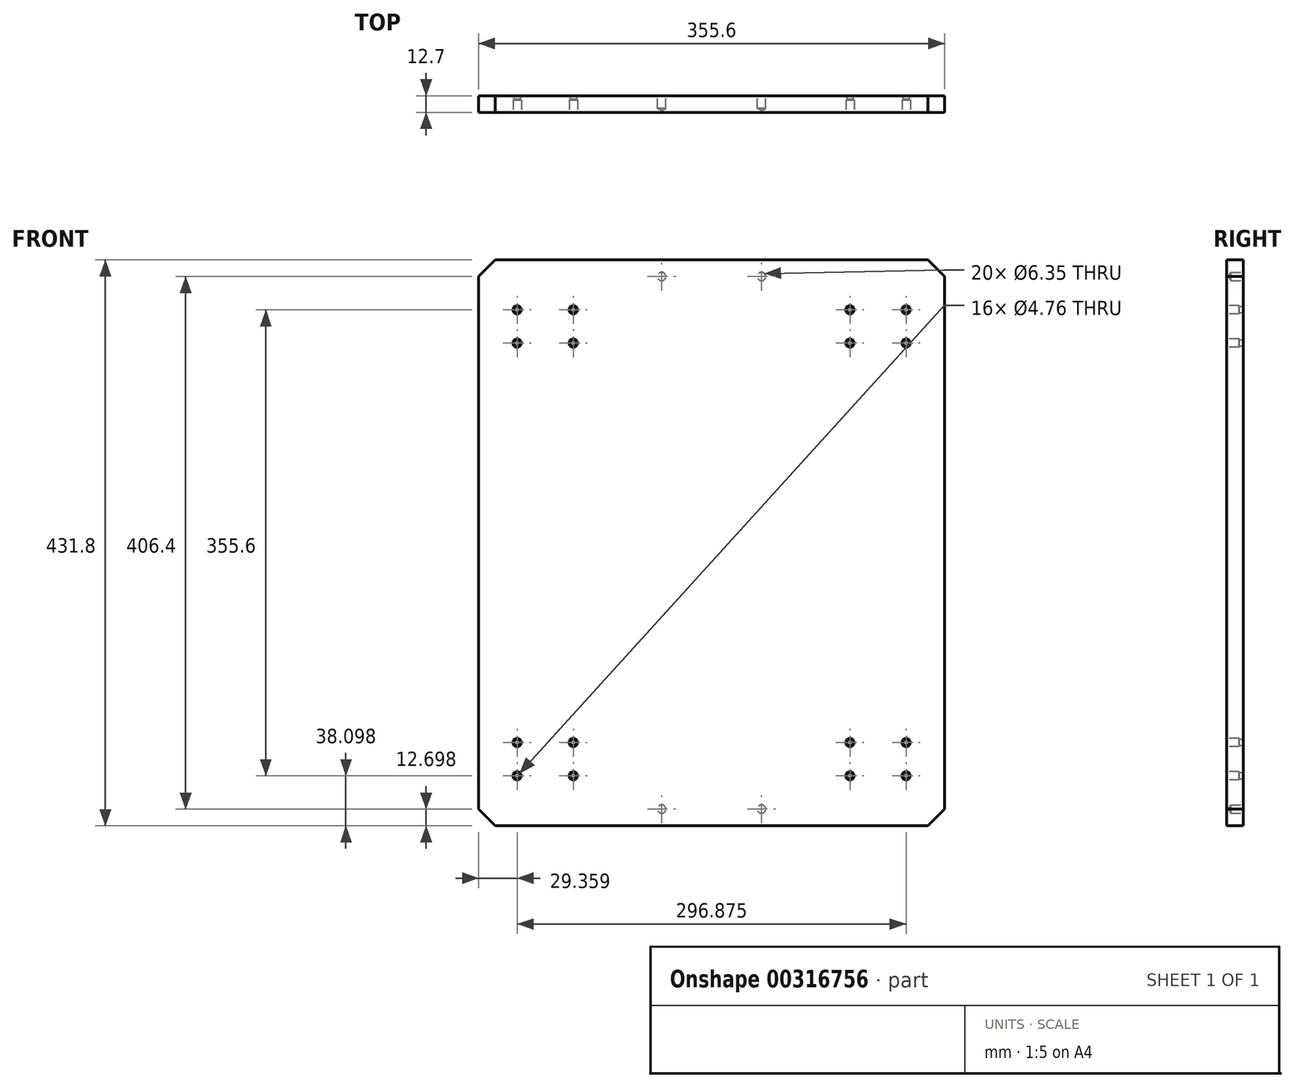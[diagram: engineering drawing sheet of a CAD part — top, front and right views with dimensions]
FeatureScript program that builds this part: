
annotation { "Feature Type Name" : "Feature", "Feature Type Description" : "" }
export const myFeature = defineFeature(function(context is Context, id is Id, definition is map)
    precondition{}
    {
        {
            var Q0;
            Q0=qCreatedBy(makeId("Front.planeOp"),FACE);
            var sketch = newSketch(context, id + "F0", { "sketchPlane" : qUnion([Q0])});
            skLineSegment(sketch, "E0.bottom", {"start": v(-92.04, 358.08) * mm, "end": v(263.56, 358.08) * mm});
            skLineSegment(sketch, "E0.top", {"start": v(-92.04, -73.72) * mm, "end": v(263.56, -73.72) * mm});
            skLineSegment(sketch, "E0.left", {"start": v(-92.04, 358.08) * mm, "end": v(-92.04, -73.72) * mm});
            skLineSegment(sketch, "E0.right", {"start": v(263.56, 358.08) * mm, "end": v(263.56, -73.72) * mm});
            skSolve(sketch);
        }
        {
            var Q0;
            Q0=makeQuery(id+"F0.imprint","IMPRINT",FACE,{"disambiguationData":[TD([[makeQuery(id+"F0.imprint","IMPRINT",EDGE,{"derivedFrom":sQuery(id+"F0.wireOp",EDGE,"E0.bottom")}),-1.0]])]});
            extrude(context, id + "F1", {"entities" : qUnion([Q0]), "depth" : 12.7 * mm});
        }
        {
            var Q0;
            Q0=makeQuery(id+"F1.opExtrude","CAP_FACE",FACE,{"disambiguationData":[OSD([sQuery(id+"F0.wireOp",EDGE,"E0.bottom"),sQuery(id+"F0.wireOp",EDGE,"E0.top"),sQuery(id+"F0.wireOp",EDGE,"E0.left"),sQuery(id+"F0.wireOp",EDGE,"E0.right")])],"isStart":false});
            var sketch = newSketch(context, id + "F2", { "sketchPlane" : qUnion([Q0])});
            skPoint(sketch, "E1", {"position": v(-62.68, -10.22) * mm});
            skPoint(sketch, "E2", {"position": v(-19.8, -35.62) * mm});
            skPoint(sketch, "E3", {"position": v(-62.68, -35.62) * mm});
            skPoint(sketch, "E4", {"position": v(-19.8, -10.22) * mm});
            skLineSegment(sketch, "E5", {"start": v(85.76, 358.08) * mm, "end": v(85.76, -73.72) * mm, "construction": true});
            skPoint(sketch, "E6.MirrorP", {"position": v(191.32, -10.22) * mm});
            skPoint(sketch, "E7.MirrorP", {"position": v(191.32, -35.62) * mm});
            skPoint(sketch, "E8.MirrorP", {"position": v(234.2, -10.22) * mm});
            skPoint(sketch, "E9.MirrorP", {"position": v(234.2, -35.62) * mm});
            skLineSegment(sketch, "E10", {"start": v(-92.04, 142.18) * mm, "end": v(263.56, 142.18) * mm, "construction": true});
            skPoint(sketch, "E11.MirrorP", {"position": v(-19.8, 294.58) * mm});
            skPoint(sketch, "E12.MirrorP", {"position": v(-19.8, 319.98) * mm});
            skPoint(sketch, "E13.MirrorP", {"position": v(-62.68, 319.98) * mm});
            skPoint(sketch, "E14.MirrorP", {"position": v(-62.68, 294.58) * mm});
            skPoint(sketch, "E15.MirrorP", {"position": v(191.32, 294.58) * mm});
            skPoint(sketch, "E16.MirrorP", {"position": v(234.2, 294.58) * mm});
            skPoint(sketch, "E17.MirrorP", {"position": v(234.2, 319.98) * mm});
            skPoint(sketch, "E18.MirrorP", {"position": v(191.32, 319.98) * mm});
            skSolve(sketch);
        }
        {
            var Q0;
            Q0=sQuery(id+"F2.wireOp",VERTEX,"E13.MirrorP");
            var Q1;
            Q1=sQuery(id+"F2.wireOp",VERTEX,"E14.MirrorP");
            var Q2;
            Q2=sQuery(id+"F2.wireOp",VERTEX,"E11.MirrorP");
            var Q3;
            Q3=sQuery(id+"F2.wireOp",VERTEX,"E12.MirrorP");
            var Q4;
            Q4=sQuery(id+"F2.wireOp",VERTEX,"E15.MirrorP");
            var Q5;
            Q5=sQuery(id+"F2.wireOp",VERTEX,"E16.MirrorP");
            var Q6;
            Q6=sQuery(id+"F2.wireOp",VERTEX,"E17.MirrorP");
            var Q7;
            Q7=sQuery(id+"F2.wireOp",VERTEX,"E18.MirrorP");
            var Q8;
            Q8=sQuery(id+"F2.wireOp",VERTEX,"E4");
            var Q9;
            Q9=sQuery(id+"F2.wireOp",VERTEX,"E1");
            var Q10;
            Q10=sQuery(id+"F2.wireOp",VERTEX,"E3");
            var Q11;
            Q11=sQuery(id+"F2.wireOp",VERTEX,"E2");
            var Q12;
            Q12=sQuery(id+"F2.wireOp",VERTEX,"E7.MirrorP");
            var Q13;
            Q13=sQuery(id+"F2.wireOp",VERTEX,"E9.MirrorP");
            var Q14;
            Q14=sQuery(id+"F2.wireOp",VERTEX,"E8.MirrorP");
            var Q15;
            Q15=sQuery(id+"F2.wireOp",VERTEX,"E6.MirrorP");
            var Q16;
            Q16=makeQuery(id+"F1.opExtrude","SWEPT_BODY",BODY,{"disambiguationData":[OSD([sQuery(id+"F0.wireOp",EDGE,"E0.bottom"),sQuery(id+"F0.wireOp",EDGE,"E0.top"),sQuery(id+"F0.wireOp",EDGE,"E0.left"),sQuery(id+"F0.wireOp",EDGE,"E0.right")])]});
            hole(context, id + "F3", {"style" : HoleStyle.SIMPLE, "endStyle" : HoleEndStyle.THROUGH, "holeDiameter" : 4.76 * mm, "tappedDepth" : 12.7 * mm, "tapClearance" : 3, "locations" : qUnion([Q0, Q1, Q2, Q3, Q4, Q5, Q6, Q7, Q8, Q9, Q10, Q11, Q12, Q13, Q14, Q15]), "scope" : qUnion([Q16])});
        }
        {
            var Q0;
            Q0=sQuery(id+"F2.wireOp",VERTEX,"E13.MirrorP");
            var Q1;
            Q1=sQuery(id+"F2.wireOp",VERTEX,"E12.MirrorP");
            var Q2;
            Q2=sQuery(id+"F2.wireOp",VERTEX,"E14.MirrorP");
            var Q3;
            Q3=sQuery(id+"F2.wireOp",VERTEX,"E11.MirrorP");
            var Q4;
            Q4=sQuery(id+"F2.wireOp",VERTEX,"E15.MirrorP");
            var Q5;
            Q5=sQuery(id+"F2.wireOp",VERTEX,"E18.MirrorP");
            var Q6;
            Q6=sQuery(id+"F2.wireOp",VERTEX,"E17.MirrorP");
            var Q7;
            Q7=sQuery(id+"F2.wireOp",VERTEX,"E16.MirrorP");
            var Q8;
            Q8=sQuery(id+"F2.wireOp",VERTEX,"E4");
            var Q9;
            Q9=sQuery(id+"F2.wireOp",VERTEX,"E2");
            var Q10;
            Q10=sQuery(id+"F2.wireOp",VERTEX,"E3");
            var Q11;
            Q11=sQuery(id+"F2.wireOp",VERTEX,"E1");
            var Q12;
            Q12=sQuery(id+"F2.wireOp",VERTEX,"E6.MirrorP");
            var Q13;
            Q13=sQuery(id+"F2.wireOp",VERTEX,"E8.MirrorP");
            var Q14;
            Q14=sQuery(id+"F2.wireOp",VERTEX,"E9.MirrorP");
            var Q15;
            Q15=sQuery(id+"F2.wireOp",VERTEX,"E7.MirrorP");
            var Q16;
            Q16=makeQuery(id+"F1.opExtrude","SWEPT_BODY",BODY,{"disambiguationData":[OSD([sQuery(id+"F0.wireOp",EDGE,"E0.bottom"),sQuery(id+"F0.wireOp",EDGE,"E0.top"),sQuery(id+"F0.wireOp",EDGE,"E0.left"),sQuery(id+"F0.wireOp",EDGE,"E0.right")])]});
            hole(context, id + "F4", {"style" : HoleStyle.SIMPLE, "endStyle" : HoleEndStyle.BLIND, "holeDiameter" : 6.35 * mm, "holeDepth" : 9.52 * mm, "tappedDepth" : 12.7 * mm, "tapClearance" : 3, "locations" : qUnion([Q0, Q1, Q2, Q3, Q4, Q5, Q6, Q7, Q8, Q9, Q10, Q11, Q12, Q13, Q14, Q15]), "scope" : qUnion([Q16])});
        }
        {
            var Q0;
            Q0=makeQuery(id+"F1.opExtrude","SWEPT_EDGE",EDGE,{"disambiguationData":[OSD([sQuery(id+"F0.wireOp",EDGE,"E0.bottom"),sQuery(id+"F0.wireOp",EDGE,"E0.left")])]});
            var Q1;
            Q1=makeQuery(id+"F1.opExtrude","SWEPT_EDGE",EDGE,{"disambiguationData":[OSD([sQuery(id+"F0.wireOp",EDGE,"E0.bottom"),sQuery(id+"F0.wireOp",EDGE,"E0.right")])]});
            var Q2;
            Q2=makeQuery(id+"F1.opExtrude","SWEPT_EDGE",EDGE,{"disambiguationData":[OSD([sQuery(id+"F0.wireOp",EDGE,"E0.top"),sQuery(id+"F0.wireOp",EDGE,"E0.right")])]});
            var Q3;
            Q3=makeQuery(id+"F1.opExtrude","SWEPT_EDGE",EDGE,{"disambiguationData":[OSD([sQuery(id+"F0.wireOp",EDGE,"E0.top"),sQuery(id+"F0.wireOp",EDGE,"E0.left")])]});
            chamfer(context, id + "F5", {"entities" : qUnion([Q0, Q1, Q2, Q3]), "width" : 12.7 * mm, "tangentPropagation" : true});
        }
        {
            var Q0;
            Q0=makeQuery(id+"F1.opExtrude","CAP_FACE",FACE,{"disambiguationData":[OSD([sQuery(id+"F0.wireOp",EDGE,"E0.bottom"),sQuery(id+"F0.wireOp",EDGE,"E0.top"),sQuery(id+"F0.wireOp",EDGE,"E0.left"),sQuery(id+"F0.wireOp",EDGE,"E0.right")])],"isStart":true});
            var sketch = newSketch(context, id + "F6", { "sketchPlane" : qUnion([Q0])});
            skPoint(sketch, "E19", {"position": v(-123.86, 345.38) * mm});
            skPoint(sketch, "E20", {"position": v(-47.66, 345.38) * mm});
            skPoint(sketch, "E21", {"position": v(-47.66, -61.02) * mm});
            skPoint(sketch, "E22", {"position": v(-123.86, -61.02) * mm});
            skSolve(sketch);
        }
        {
            var Q0;
            Q0=sQuery(id+"F6.wireOp",VERTEX,"E19");
            var Q1;
            Q1=sQuery(id+"F6.wireOp",VERTEX,"E20");
            var Q2;
            Q2=sQuery(id+"F6.wireOp",VERTEX,"E21");
            var Q3;
            Q3=sQuery(id+"F6.wireOp",VERTEX,"E22");
            var Q4;
            Q4=makeQuery(id+"F1.opExtrude","SWEPT_BODY",BODY,{"disambiguationData":[OSD([sQuery(id+"F0.wireOp",EDGE,"E0.bottom"),sQuery(id+"F0.wireOp",EDGE,"E0.top"),sQuery(id+"F0.wireOp",EDGE,"E0.left"),sQuery(id+"F0.wireOp",EDGE,"E0.right")])]});
            hole(context, id + "F7", {"style" : HoleStyle.SIMPLE, "endStyle" : HoleEndStyle.BLIND, "holeDiameter" : 6.35 * mm, "holeDepth" : 9.52 * mm, "tappedDepth" : 12.7 * mm, "tapClearance" : 3, "locations" : qUnion([Q0, Q1, Q2, Q3]), "scope" : qUnion([Q4])});
        }
    });
